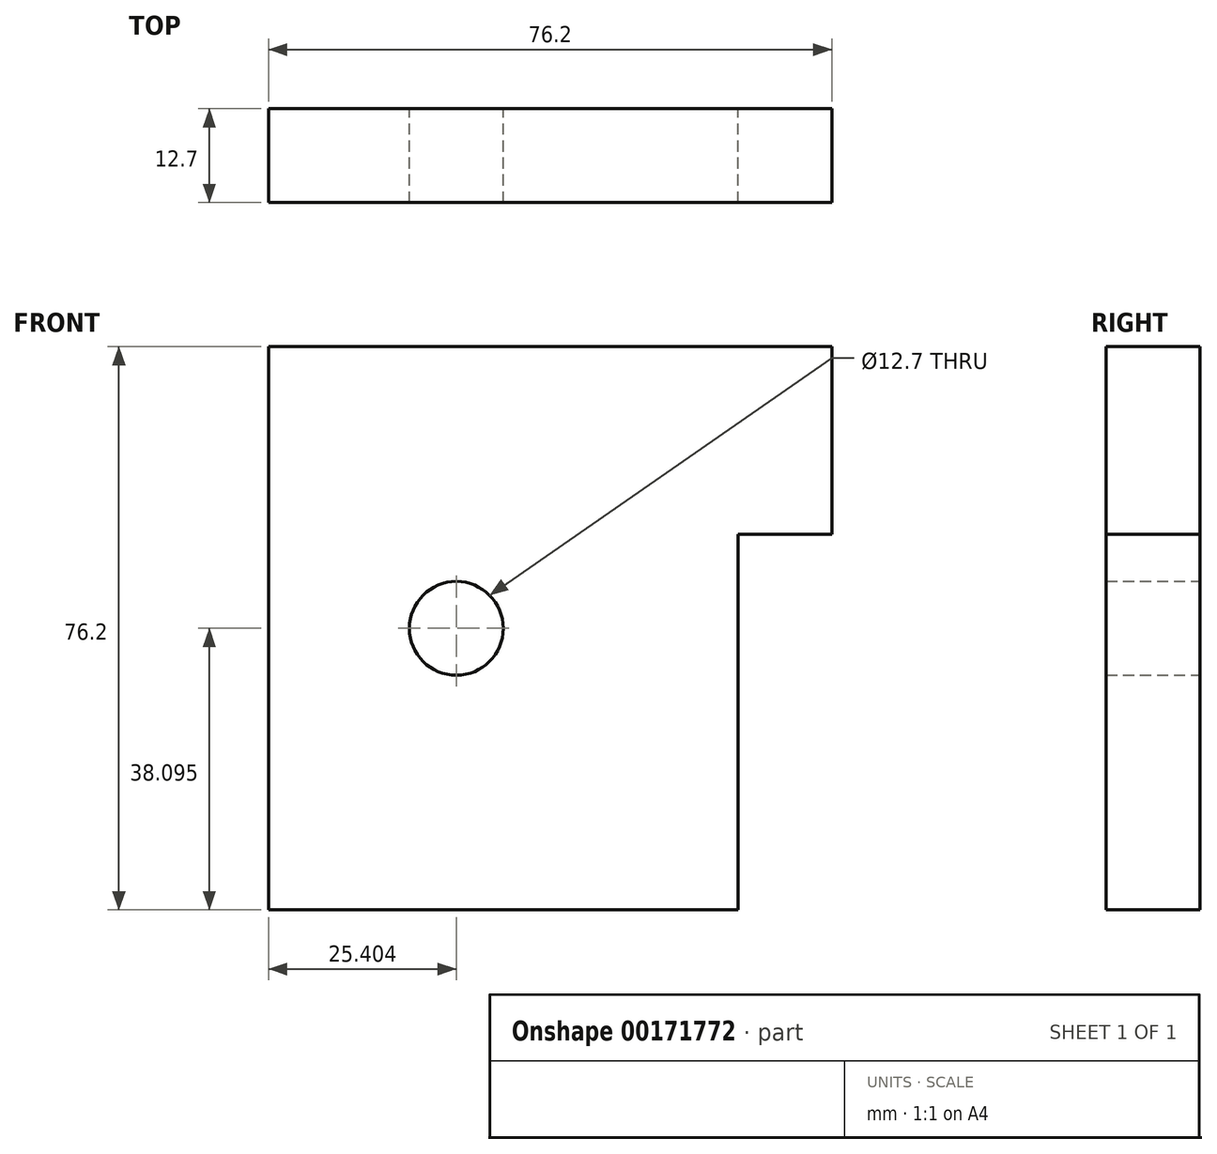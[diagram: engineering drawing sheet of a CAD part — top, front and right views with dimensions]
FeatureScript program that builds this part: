
annotation { "Feature Type Name" : "Feature", "Feature Type Description" : "" }
export const myFeature = defineFeature(function(context is Context, id is Id, definition is map)
    precondition{}
    {
        {
            var Q0;
            Q0=qCreatedBy(makeId("Front.planeOp"),FACE);
            var sketch = newSketch(context, id + "F0", { "sketchPlane" : qUnion([Q0])});
            skLineSegment(sketch, "E0", {"start": v(-53.82, 29.96) * mm, "end": v(22.38, 29.96) * mm});
            skLineSegment(sketch, "E1", {"start": v(22.38, 29.96) * mm, "end": v(22.38, 4.56) * mm});
            skLineSegment(sketch, "E2", {"start": v(22.38, 4.56) * mm, "end": v(9.68, 4.56) * mm});
            skLineSegment(sketch, "E3", {"start": v(9.68, 4.56) * mm, "end": v(9.68, -46.24) * mm});
            skLineSegment(sketch, "E4", {"start": v(9.68, -46.24) * mm, "end": v(-53.82, -46.24) * mm});
            skLineSegment(sketch, "E5", {"start": v(-53.82, -46.24) * mm, "end": v(-53.82, 29.96) * mm});
            skCircle(sketch, "E6", {"center": v(-28.42, -8.14) * mm, "radius": 6.35 * mm});
            skSolve(sketch);
        }
        {
            var Q0;
            Q0=makeQuery(id+"F0.imprint","IMPRINT",FACE,{"disambiguationData":[TD([[makeQuery(id+"F0.imprint","IMPRINT",EDGE,{"derivedFrom":sQuery(id+"F0.wireOp",EDGE,"E0")}),-1.0]])]});
            extrude(context, id + "F1", {"entities" : qUnion([Q0]), "depth" : 12.7 * mm});
        }
    });
